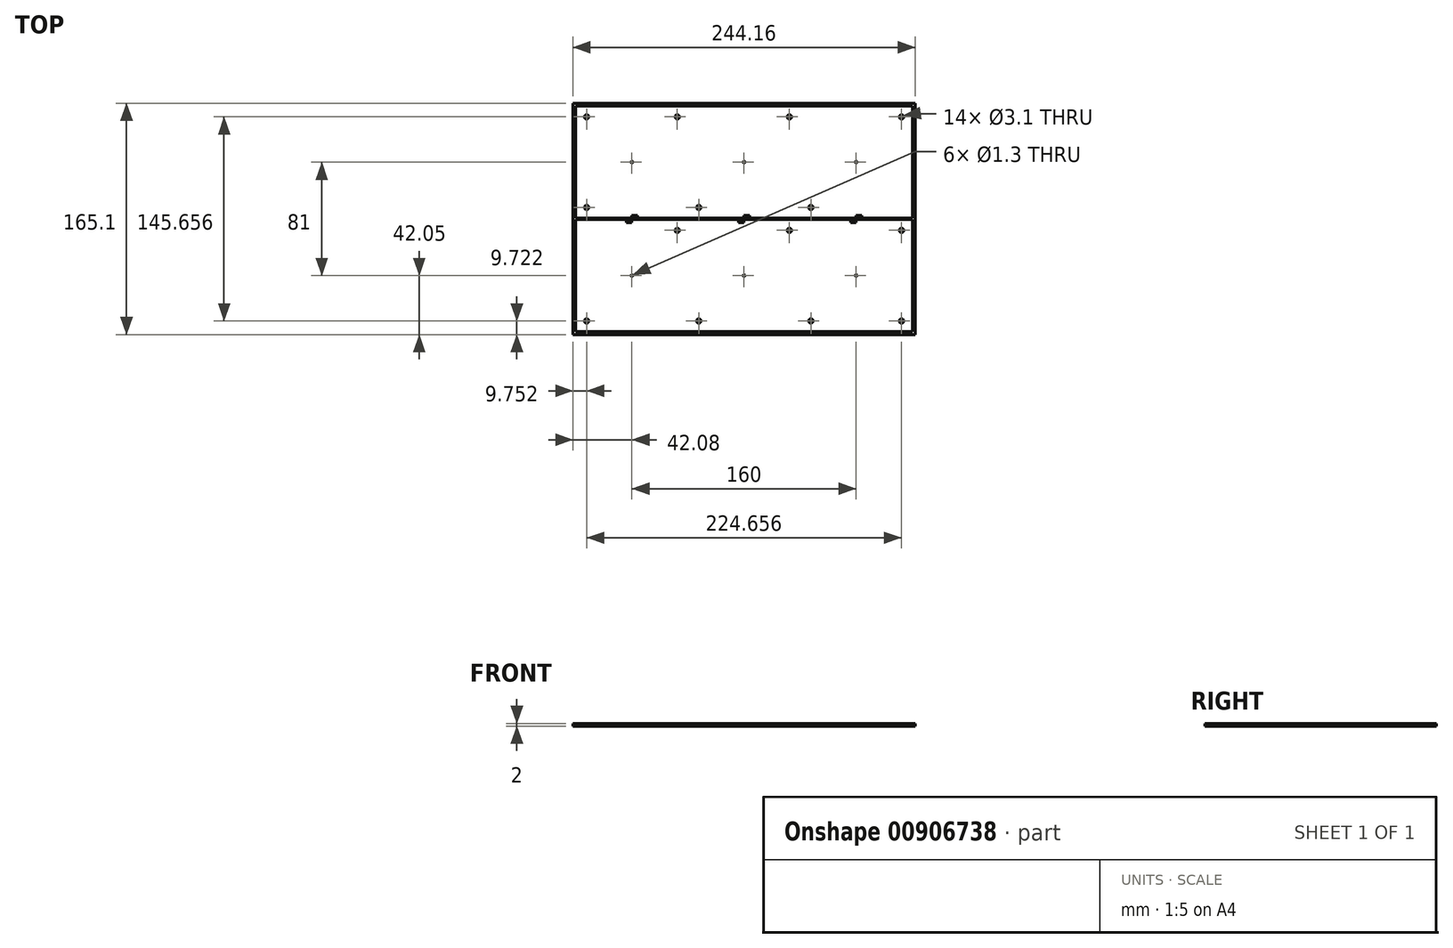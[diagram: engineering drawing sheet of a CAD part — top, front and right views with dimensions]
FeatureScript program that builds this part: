
annotation { "Feature Type Name" : "Feature", "Feature Type Description" : "" }
export const myFeature = defineFeature(function(context is Context, id is Id, definition is map)
    precondition{}
    {
        {
            var Q0;
            Q0=qCreatedBy(makeId("Top.planeOp"),FACE);
            var sketch = newSketch(context, id + "F0", { "sketchPlane" : qUnion([Q0])});
            skLineSegment(sketch, "E0.bottom", {"start": v(-122.07, 82.55) * mm, "end": v(122.08, 82.55) * mm});
            skLineSegment(sketch, "E0.top", {"start": v(-122.08, -82.55) * mm, "end": v(122.07, -82.55) * mm});
            skLineSegment(sketch, "E0.left", {"start": v(-122.07, 82.55) * mm, "end": v(-122.08, -82.55) * mm});
            skLineSegment(sketch, "E0.right", {"start": v(122.08, 82.55) * mm, "end": v(122.07, -82.55) * mm});
            skPoint(sketch, "E0.middle", {"position": v(0, 0) * mm});
            skSolve(sketch);
        }
        {
            var Q0;
            Q0 = qSketchRegion(id + "F0", true);
            extrude(context, id + "F1", {"entities" : qUnion([Q0]), "depth" : 2 * mm, "offsetDistance" : 25 * mm});
        }
        {
            var Q0;
            Q0=makeQuery(id+"F1.opExtrude","CAP_FACE",FACE,{"disambiguationData":[OSD([sQuery(id+"F0.wireOp",EDGE,"E0.bottom"),sQuery(id+"F0.wireOp",EDGE,"E0.top"),sQuery(id+"F0.wireOp",EDGE,"E0.left"),sQuery(id+"F0.wireOp",EDGE,"E0.right")])],"isStart":false});
            var sketch = newSketch(context, id + "F2", { "sketchPlane" : qUnion([Q0])});
            skLineSegment(sketch, "E1", {"start": v(-120.07, 80.55) * mm, "end": v(-120.08, 1) * mm});
            skLineSegment(sketch, "E2", {"start": v(120.07, -80.55) * mm, "end": v(120.08, -1) * mm});
            skLineSegment(sketch, "E3", {"start": v(-120.07, 80.55) * mm, "end": v(120.08, 80.55) * mm});
            skLineSegment(sketch, "E4", {"start": v(-120.08, -80.55) * mm, "end": v(120.07, -80.55) * mm});
            skLineSegment(sketch, "E5", {"start": v(-120.08, 0.5) * mm, "end": v(120.08, 0.5) * mm});
            skLineSegment(sketch, "E6", {"start": v(-120.08, -0.5) * mm, "end": v(120.08, -0.5) * mm});
            skLineSegment(sketch, "E7.trimOffspring", {"start": v(120.08, 1) * mm, "end": v(120.08, 80.55) * mm});
            skLineSegment(sketch, "E8.trimOffspring", {"start": v(-120.08, -1) * mm, "end": v(-120.08, -80.55) * mm});
            skLineSegment(sketch, "E9", {"start": v(120.08, 1) * mm, "end": v(120.08, 0.5) * mm});
            skLineSegment(sketch, "E10", {"start": v(-120.08, 1) * mm, "end": v(-120.08, 0.5) * mm});
            skLineSegment(sketch, "E11", {"start": v(-120.08, -0.5) * mm, "end": v(-120.08, -1) * mm});
            skLineSegment(sketch, "E12", {"start": v(120.08, -1) * mm, "end": v(120.08, -0.5) * mm});
            skSolve(sketch);
        }
        {
            var Q0;
            Q0 = qSketchRegion(id + "F2", true);
            extrude(context, id + "F3", {"entities" : qUnion([Q0]), "operationType" : NewBodyOperationType.REMOVE, "oppositeDirection" : true, "depth" : 1 * mm, "offsetDistance" : 25 * mm});
        }
        {
            var Q0;
            Q0=makeQuery(id+"F3.boolean.opBoolean","COPY",FACE,{"derivedFrom":makeQuery(id+"F3.opExtrude","CAP_FACE",FACE,{"disambiguationData":[OSD([sQuery(id+"F2.wireOp",EDGE,"E1"),sQuery(id+"F2.wireOp",EDGE,"E3"),sQuery(id+"F2.wireOp",EDGE,"E5"),sQuery(id+"F2.wireOp",EDGE,"E7.trimOffspring"),sQuery(id+"F2.wireOp",EDGE,"E9"),sQuery(id+"F2.wireOp",EDGE,"E10")])],"isStart":false})});
            var Q1;
            Q1=makeQuery(id+"F3.boolean.opBoolean","COPY",FACE,{"derivedFrom":makeQuery(id+"F3.opExtrude","CAP_FACE",FACE,{"disambiguationData":[OSD([sQuery(id+"F2.wireOp",EDGE,"E1"),sQuery(id+"F2.wireOp",EDGE,"E3"),sQuery(id+"F2.wireOp",EDGE,"E5"),sQuery(id+"F2.wireOp",EDGE,"E7.trimOffspring"),sQuery(id+"F2.wireOp",EDGE,"E9"),sQuery(id+"F2.wireOp",EDGE,"E10")])],"isStart":false})});
            var Q2;
            Q2=makeQuery(id+"F3.boolean.opBoolean","COPY",FACE,{"derivedFrom":makeQuery(id+"F3.opExtrude","CAP_FACE",FACE,{"disambiguationData":[OSD([sQuery(id+"F2.wireOp",EDGE,"E1"),sQuery(id+"F2.wireOp",EDGE,"E3"),sQuery(id+"F2.wireOp",EDGE,"E5"),sQuery(id+"F2.wireOp",EDGE,"E7.trimOffspring"),sQuery(id+"F2.wireOp",EDGE,"E9"),sQuery(id+"F2.wireOp",EDGE,"E10")])],"isStart":false})});
            var sketch = newSketch(context, id + "F4", { "sketchPlane" : qUnion([Q0, Q1, Q2])});
            skLineSegment(sketch, "E13", {"start": v(-40, -80.55) * mm, "end": v(-40, -0.5) * mm});
            skLineSegment(sketch, "E14", {"start": v(40, -80.55) * mm, "end": v(40, -0.5) * mm});
            skCircle(sketch, "E15", {"center": v(-47.67, 72.83) * mm, "radius": 1.55 * mm});
            skCircle(sketch, "E16", {"center": v(32.33, 72.83) * mm, "radius": 1.55 * mm});
            skCircle(sketch, "E17", {"center": v(112.33, 72.83) * mm, "radius": 1.55 * mm});
            skCircle(sketch, "E18", {"center": v(-112.33, 8.17) * mm, "radius": 1.55 * mm});
            skCircle(sketch, "E19", {"center": v(-32.33, 8.17) * mm, "radius": 1.55 * mm});
            skCircle(sketch, "E20", {"center": v(47.67, 8.17) * mm, "radius": 1.55 * mm});
            skCircle(sketch, "E21", {"center": v(-80, 40.5) * mm, "radius": 0.65 * mm});
            skCircle(sketch, "E22", {"center": v(0, 40.5) * mm, "radius": 0.65 * mm});
            skCircle(sketch, "E23", {"center": v(80, 40.5) * mm, "radius": 0.65 * mm});
            skCircle(sketch, "E24", {"center": v(-112.33, -72.83) * mm, "radius": 1.55 * mm});
            skCircle(sketch, "E25", {"center": v(-32.33, -72.83) * mm, "radius": 1.55 * mm});
            skCircle(sketch, "E26", {"center": v(47.67, -72.83) * mm, "radius": 1.55 * mm});
            skCircle(sketch, "E27", {"center": v(112.33, -8.17) * mm, "radius": 1.55 * mm});
            skCircle(sketch, "E28", {"center": v(32.33, -8.17) * mm, "radius": 1.55 * mm});
            skCircle(sketch, "E29", {"center": v(-47.67, -8.17) * mm, "radius": 1.55 * mm});
            skCircle(sketch, "E30", {"center": v(0, -40.5) * mm, "radius": 0.65 * mm});
            skCircle(sketch, "E31", {"center": v(80, -40.5) * mm, "radius": 0.65 * mm});
            skCircle(sketch, "E32", {"center": v(112.33, -72.83) * mm, "radius": 1.55 * mm});
            skCircle(sketch, "E33", {"center": v(-112.33, 72.83) * mm, "radius": 1.55 * mm});
            skCircle(sketch, "E34", {"center": v(-80, -40.5) * mm, "radius": 0.65 * mm});
            skLineSegment(sketch, "E35.bottom", {"start": v(-80, -0.5) * mm, "end": v(-83.9, -0.5) * mm});
            skLineSegment(sketch, "E35.top", {"start": v(-80, -2.61) * mm, "end": v(-83.9, -2.61) * mm});
            skLineSegment(sketch, "E35.left", {"start": v(-80, -0.5) * mm, "end": v(-80, -2.61) * mm});
            skLineSegment(sketch, "E35.right", {"start": v(-83.9, -0.5) * mm, "end": v(-83.9, -2.61) * mm});
            skLineSegment(sketch, "E36.bottom", {"start": v(-80, 0.5) * mm, "end": v(-76.1, 0.5) * mm});
            skLineSegment(sketch, "E36.top", {"start": v(-80, 2.61) * mm, "end": v(-76.1, 2.61) * mm});
            skLineSegment(sketch, "E36.left", {"start": v(-80, 0.5) * mm, "end": v(-80, 2.61) * mm});
            skLineSegment(sketch, "E36.right", {"start": v(-76.1, 0.5) * mm, "end": v(-76.1, 2.61) * mm});
            skLineSegment(sketch, "E37.bottom", {"start": v(0, -0.5) * mm, "end": v(-3.9, -0.5) * mm});
            skLineSegment(sketch, "E37.top", {"start": v(0, -2.62) * mm, "end": v(-3.9, -2.62) * mm});
            skLineSegment(sketch, "E37.left", {"start": v(0, -0.5) * mm, "end": v(0, -2.62) * mm});
            skLineSegment(sketch, "E37.right", {"start": v(-3.9, -0.5) * mm, "end": v(-3.9, -2.62) * mm});
            skLineSegment(sketch, "E38.bottom", {"start": v(0, 0.5) * mm, "end": v(3.9, 0.5) * mm});
            skLineSegment(sketch, "E38.top", {"start": v(0, 2.61) * mm, "end": v(3.9, 2.61) * mm});
            skLineSegment(sketch, "E38.left", {"start": v(0, 0.5) * mm, "end": v(0, 2.61) * mm});
            skLineSegment(sketch, "E38.right", {"start": v(3.9, 0.5) * mm, "end": v(3.9, 2.62) * mm});
            skLineSegment(sketch, "E39.bottom", {"start": v(80, -0.5) * mm, "end": v(76.1, -0.5) * mm});
            skLineSegment(sketch, "E39.top", {"start": v(80, -2.61) * mm, "end": v(76.1, -2.61) * mm});
            skLineSegment(sketch, "E39.left", {"start": v(80, -0.5) * mm, "end": v(80, -2.61) * mm});
            skLineSegment(sketch, "E39.right", {"start": v(76.1, -0.5) * mm, "end": v(76.1, -2.61) * mm});
            skLineSegment(sketch, "E40.bottom", {"start": v(80, 0.5) * mm, "end": v(83.9, 0.5) * mm});
            skLineSegment(sketch, "E40.top", {"start": v(80, 2.62) * mm, "end": v(83.9, 2.62) * mm});
            skLineSegment(sketch, "E40.left", {"start": v(80, 0.5) * mm, "end": v(80, 2.62) * mm});
            skLineSegment(sketch, "E40.right", {"start": v(83.9, 0.5) * mm, "end": v(83.9, 2.62) * mm});
            skSolve(sketch);
        }
        {
            var Q0;
            Q0 = qSketchRegion(id + "F4", true);
            extrude(context, id + "F5", {"entities" : qUnion([Q0]), "operationType" : NewBodyOperationType.REMOVE, "endBound" : BoundingType.THROUGH_ALL, "oppositeDirection" : true, "depth" : 25 * mm, "offsetDistance" : 25 * mm});
        }
    });
